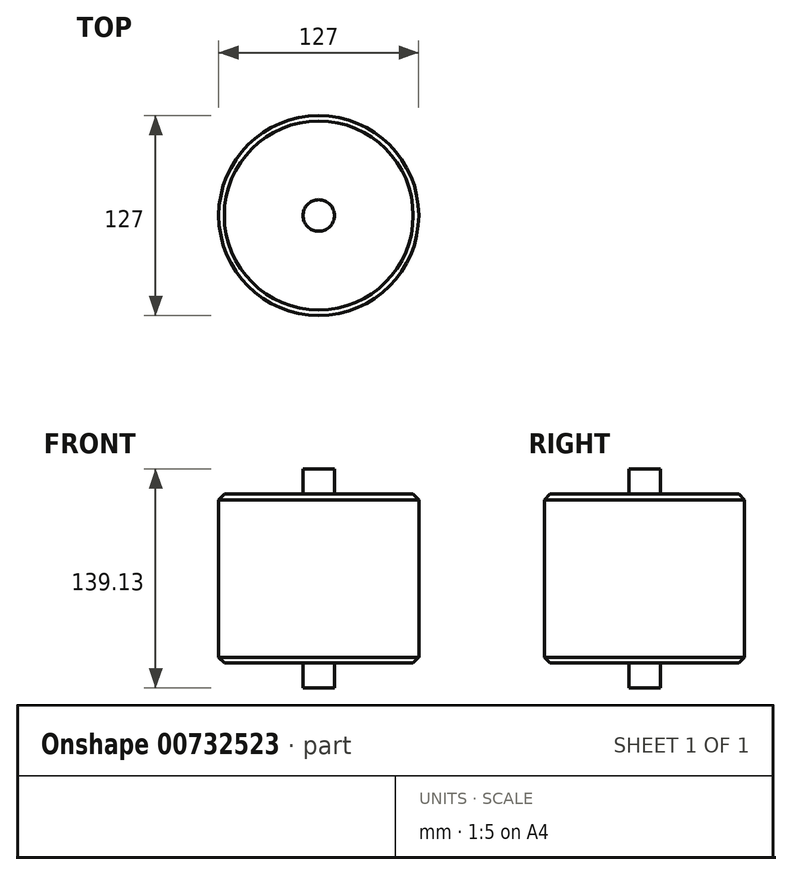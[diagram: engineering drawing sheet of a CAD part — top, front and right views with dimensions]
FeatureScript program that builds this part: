
annotation { "Feature Type Name" : "Feature", "Feature Type Description" : "" }
export const myFeature = defineFeature(function(context is Context, id is Id, definition is map)
    precondition{}
    {
        {
            var Q0;
            Q0=qCreatedBy(makeId("Front.planeOp"),FACE);
            var sketch = newSketch(context, id + "F0", { "sketchPlane" : qUnion([Q0])});
            skLineSegment(sketch, "E0", {"start": v(0, 62.05) * mm, "end": v(10, 62.05) * mm});
            skLineSegment(sketch, "E1", {"start": v(10, 62.05) * mm, "end": v(10, 46.05) * mm});
            skLineSegment(sketch, "E2", {"start": v(10, 46.05) * mm, "end": v(60, 46.05) * mm});
            skLineSegment(sketch, "E3", {"start": v(60, 46.05) * mm, "end": v(63.5, 42.48) * mm});
            skLineSegment(sketch, "E4", {"start": v(63.5, 42.48) * mm, "end": v(63.5, -57.52) * mm});
            skLineSegment(sketch, "E5", {"start": v(63.5, -57.52) * mm, "end": v(60, -61.08) * mm});
            skLineSegment(sketch, "E6", {"start": v(60, -61.08) * mm, "end": v(10, -61.08) * mm});
            skLineSegment(sketch, "E7", {"start": v(10, -61.08) * mm, "end": v(10, -77.08) * mm});
            skLineSegment(sketch, "E8", {"start": v(10, -77.08) * mm, "end": v(0, -77.08) * mm});
            skLineSegment(sketch, "E9", {"start": v(0, 62.05) * mm, "end": v(0, -77.08) * mm});
            skSolve(sketch);
        }
        {
            var Q0;
            Q0=makeQuery(id+"F0.imprint","IMPRINT",FACE,{"disambiguationData":[TD([[makeQuery(id+"F0.imprint","IMPRINT",EDGE,{"derivedFrom":sQuery(id+"F0.wireOp",EDGE,"E0")}),-1.0]])]});
            var Q1;
            Q1=sQuery(id+"F0.wireOp",EDGE,"E9");
            revolve(context, id + "F1", {"surfaceOperationType" : NewSurfaceOperationType.NEW, "entities" : qUnion([Q0]), "axis" : qUnion([Q1]), "revolveType" : RevolveType.FULL});
        }
    });
